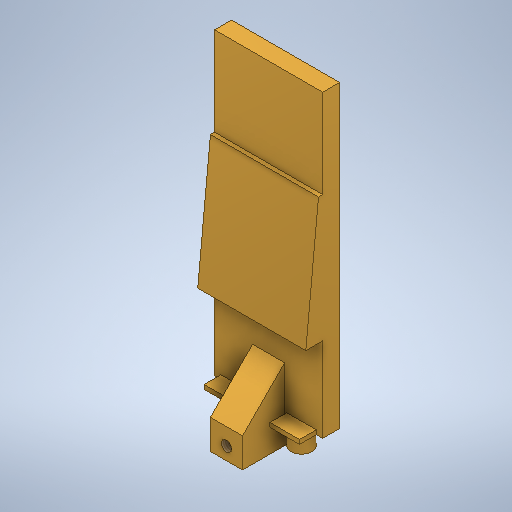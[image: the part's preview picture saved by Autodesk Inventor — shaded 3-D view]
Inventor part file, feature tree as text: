
AUTODESK INVENTOR PART (.ipt)
format: ipt  version: 2025 (Build 290162010, 162A)  size: 368,128 bytes
history: native  units: mm
features: sketch x7, extrude x6, chamfer x2, hole x1, projected_geometry x1
ambient origin geometry x8: Origin, YZ Plane, XZ Plane, XY Plane, X Axis, Y Axis, Z Axis, Center Point
bodies: Volumenkörper1 (feature_tree)
feature tree (17):
  extrude  "Extrusion1"  Depth=25.6mm
  extrude  "Extrusion2"  Depth=5.0mm
  extrude  "Extrusion3"  Depth=5.0mm
  chamfer  "Fasen1"  Distance=5.0mm
  extrude  "Extrusion4"  Depth=77.0mm
  extrude  "Extrusion5"  Depth=6.0mm
  extrude  "Extrusion6"  Depth=6.0mm
  hole  "Bohrung1"  [1 undecoded]
  chamfer  "Fasen2"  Distance=16.0mm
  sketch  "Skizze1"  dims[d7=4.0mm d8=0.0mm d9=25.6mm]
  sketch  "Skizze2"  dims[d18=2.459mm d19=6.0mm d20=4.0mm d21=2.0mm d22=90.0deg d23=8.0mm d24=20.594885mm d29=5.0mm]
  sketch  "Skizze3"  dims[d31=4.0mm d32=0.0mm d34=40.0mm d35=5.0mm d36=0.0mm]
  sketch  "Skizze4"  dims[d39=40.0mm d40=4.0mm d41=45.0deg d48=77.0mm]
  sketch  "Skizze5"  dims[d49=9.0mm d50=6.0mm]
  projected_geometry  "Projizierte Kontur1"
  sketch  "Skizze6"  dims[d51=9.0mm d52=6.0mm]
  sketch  "Skizze7"  dims[d53=3.0mm d54=5.0mm d57=16.0mm d58=10.0mm d59=0.0mm d60=7.0mm d61=1.0mm d62=7.0mm d63=1.0mm d64=4.0mm d65=0.0mm d66=4.0mm d69=5.0mm d70=5.0mm d71=7.0mm d72=10.0mm d73=0.0mm d74=10.0mm d75=2.0mm d76=45.0deg]
note: 1 required parameter value undecoded (feature->parameter linkage not recoverable at this tier; creation-order binding heuristic only, values carry confidence <= 0.55)
